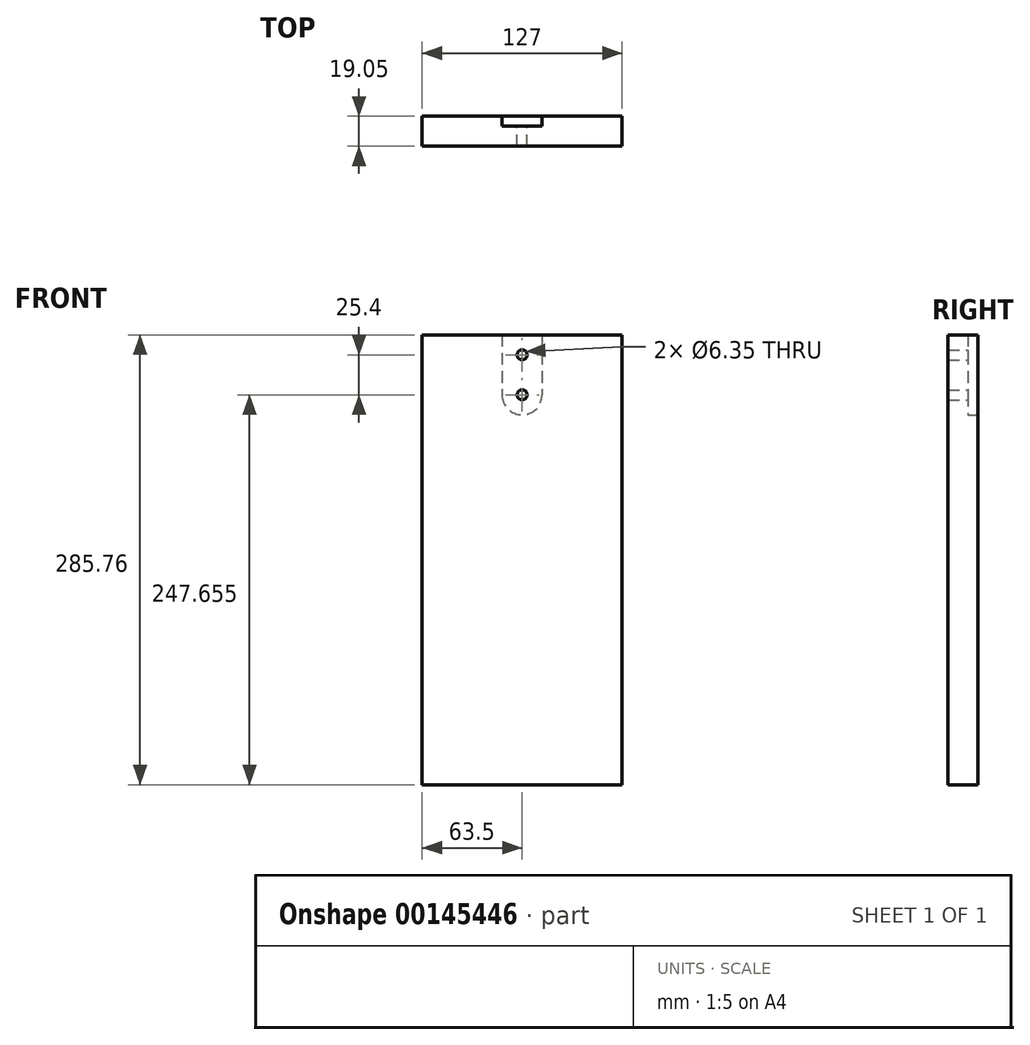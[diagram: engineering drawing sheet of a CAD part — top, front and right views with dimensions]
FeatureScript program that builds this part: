
annotation { "Feature Type Name" : "Feature", "Feature Type Description" : "" }
export const myFeature = defineFeature(function(context is Context, id is Id, definition is map)
    precondition{}
    {
        {
            var Q0;
            Q0=qCreatedBy(makeId("Front.planeOp"),FACE);
            var sketch = newSketch(context, id + "F0", { "sketchPlane" : qUnion([Q0])});
            skLineSegment(sketch, "E0.bottom", {"start": v(-63.5, 142.87) * mm, "end": v(63.5, 142.88) * mm});
            skLineSegment(sketch, "E0.top", {"start": v(-63.5, -142.88) * mm, "end": v(63.5, -142.88) * mm});
            skLineSegment(sketch, "E0.left", {"start": v(-63.5, 142.88) * mm, "end": v(-63.5, -142.88) * mm});
            skLineSegment(sketch, "E0.right", {"start": v(63.5, 142.88) * mm, "end": v(63.5, -142.88) * mm});
            skPoint(sketch, "E0.middle", {"position": v(0, 0) * mm});
            skCircle(sketch, "E1", {"center": v(0, 168.28) * mm, "radius": 279.4 * mm, "construction": true});
            skPoint(sketch, "E1.centerSnap0", {"position": v(0, 142.88) * mm});
            skSolve(sketch);
        }
        {
            var Q0;
            Q0=qSketchRegion(id+"F0",true);
            extrude(context, id + "F1", {"entities" : qUnion([Q0]), "depth" : 19.05 * mm});
        }
        {
            var Q0;
            Q0=makeQuery(id+"F1.opExtrude","CAP_FACE",FACE,{"disambiguationData":[OSD([sQuery(id+"F0.wireOp",EDGE,"E0.bottom"),sQuery(id+"F0.wireOp",EDGE,"E0.top"),sQuery(id+"F0.wireOp",EDGE,"E0.left"),sQuery(id+"F0.wireOp",EDGE,"E0.right")])],"isStart":true});
            var sketch = newSketch(context, id + "F2", { "sketchPlane" : qUnion([Q0])});
            skArc(sketch, "E2", {"start": v(12.7, 142.88) * mm, "mid": v(0, 155.57) * mm, "end": v(-12.7, 142.88) * mm});
            skArc(sketch, "E3", {"start": v(-12.7, 104.77) * mm, "mid": v(0, 92.07) * mm, "end": v(12.7, 104.77) * mm});
            skLineSegment(sketch, "E4", {"start": v(-12.7, 142.88) * mm, "end": v(-12.7, 104.77) * mm});
            skLineSegment(sketch, "E5", {"start": v(12.7, 142.88) * mm, "end": v(12.7, 104.77) * mm});
            skSolve(sketch);
        }
        {
            var Q0;
            Q0=qSketchRegion(id+"F2",true);
            extrude(context, id + "F3", {"entities" : qUnion([Q0]), "operationType" : NewBodyOperationType.REMOVE, "oppositeDirection" : true, "depth" : 6.35 * mm});
        }
        {
            var Q0;
            Q0=makeQuery(id+"F3.boolean.opBoolean","COPY",FACE,{"derivedFrom":makeQuery(id+"F3.opExtrude","CAP_FACE",FACE,{"disambiguationData":[OSD([sQuery(id+"F2.wireOp",EDGE,"E2"),sQuery(id+"F2.wireOp",EDGE,"E3"),sQuery(id+"F2.wireOp",EDGE,"E4"),sQuery(id+"F2.wireOp",EDGE,"E5")])],"isStart":false})});
            var sketch = newSketch(context, id + "F4", { "sketchPlane" : qUnion([Q0])});
            skCircle(sketch, "E6", {"center": v(0, 104.77) * mm, "radius": 3.18 * mm});
            skCircle(sketch, "E7", {"center": v(0, 130.17) * mm, "radius": 3.18 * mm});
            skSolve(sketch);
        }
        {
            var Q0;
            Q0=qSketchRegion(id+"F4",true);
            extrude(context, id + "F5", {"entities" : qUnion([Q0]), "operationType" : NewBodyOperationType.REMOVE, "endBound" : BoundingType.THROUGH_ALL, "oppositeDirection" : true, "depth" : 25.4 * mm});
        }
    });
